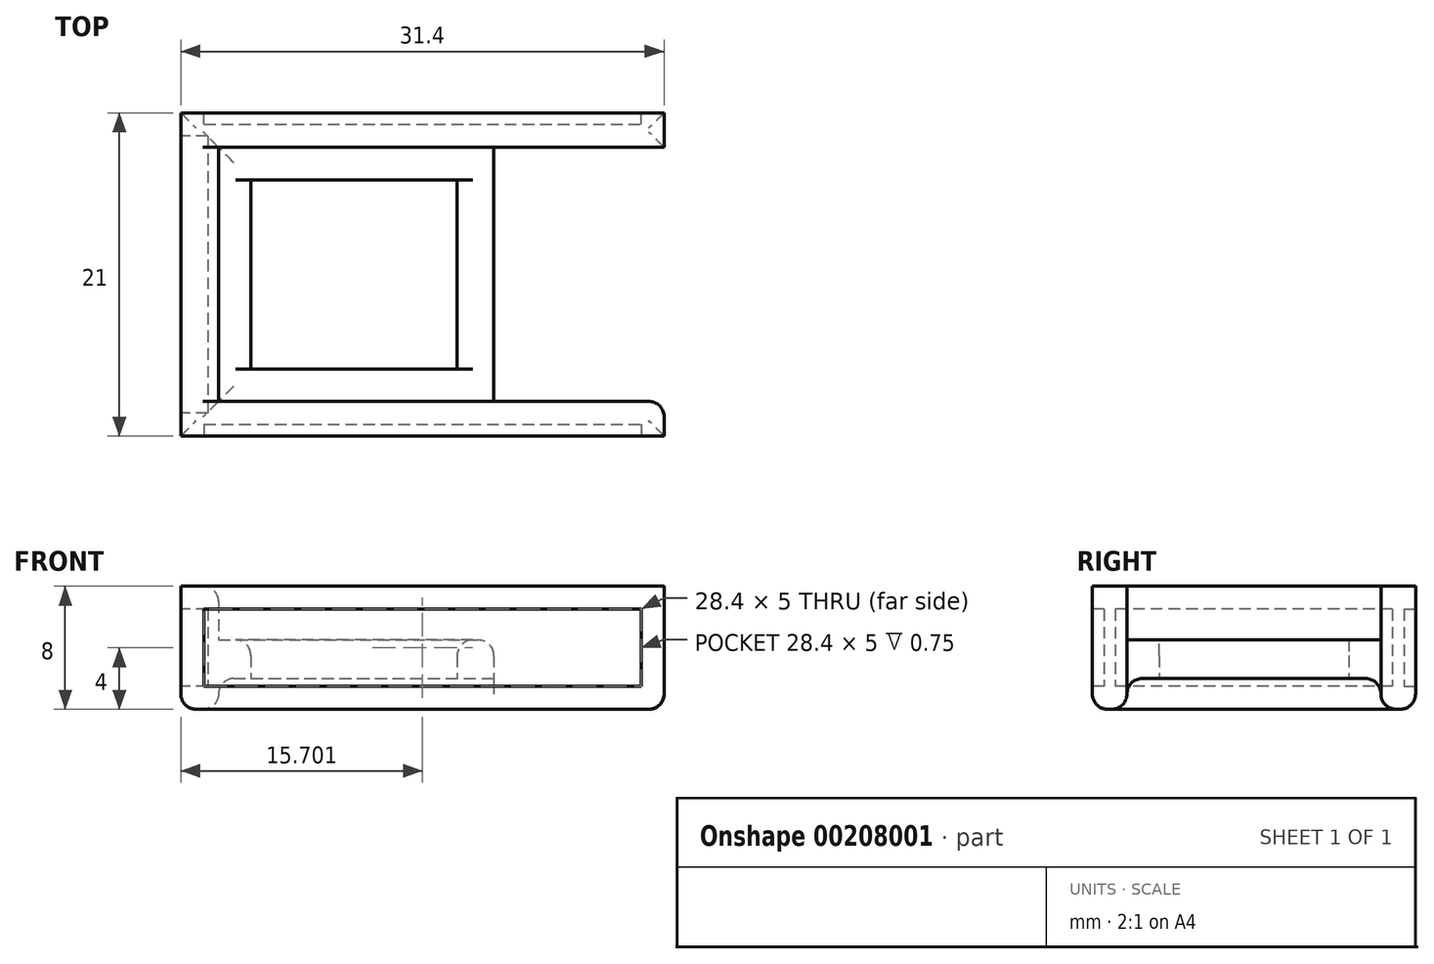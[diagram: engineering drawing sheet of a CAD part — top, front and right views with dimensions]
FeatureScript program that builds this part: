
annotation { "Feature Type Name" : "Feature", "Feature Type Description" : "" }
export const myFeature = defineFeature(function(context is Context, id is Id, definition is map)
    precondition{}
    {
        {
            var Q0;
            Q0=qCreatedBy(makeId("Top.planeOp"),FACE);
            var sketch = newSketch(context, id + "F0", { "sketchPlane" : qUnion([Q0])});
            skLineSegment(sketch, "E0.right", {"start": v(-20, 11.13) * mm, "end": v(-20, -11.87) * mm});
            skLineSegment(sketch, "E1", {"start": v(9.95, 7.88) * mm, "end": v(9.95, -8.62) * mm});
            skPoint(sketch, "E2.orphan", {"position": v(-20, -0.37) * mm});
            skPoint(sketch, "E3.end.orphan", {"position": v(-16.55, -1.12) * mm});
            skLineSegment(sketch, "E4", {"start": v(-16.55, 7.88) * mm, "end": v(-16.55, -8.62) * mm});
            skLineSegment(sketch, "E5", {"start": v(13.4, 11.13) * mm, "end": v(13.4, -11.87) * mm});
            skLineSegment(sketch, "E6", {"start": v(-20, 11.13) * mm, "end": v(13.4, 11.13) * mm});
            skLineSegment(sketch, "E7", {"start": v(-20, -11.87) * mm, "end": v(13.4, -11.87) * mm});
            skLineSegment(sketch, "E8", {"start": v(-16.55, 7.88) * mm, "end": v(9.95, 7.88) * mm});
            skLineSegment(sketch, "E9", {"start": v(-16.55, -8.62) * mm, "end": v(9.95, -8.62) * mm});
            skLineSegment(sketch, "E10", {"start": v(1.34, 7.88) * mm, "end": v(1.34, -8.62) * mm});
            skSolve(sketch);
        }
        {
            var Q0;
            Q0=makeQuery(id+"F0.imprint","IMPRINT",FACE,{"disambiguationData":[TD([[makeQuery(id+"F0.imprint","IMPRINT",EDGE,{"derivedFrom":sQuery(id+"F0.wireOp",EDGE,"E0.right")}),1.0]])]});
            extrude(context, id + "F1", {"entities" : qUnion([Q0]), "depth" : 8 * mm});
        }
        {
            var Q0;
            {var subQ0=sQuery(id+"F0.wireOp",EDGE,"E4");Q0=makeQuery(id+"F0.imprint","IMPRINT",FACE,{"disambiguationData":[TD([[makeQuery(id+"F0.imprint","IMPRINT",EDGE,{"derivedFrom":subQ0}),1.0]])]});}
            extrude(context, id + "F2", {"entities" : qUnion([Q0]), "operationType" : NewBodyOperationType.ADD, "depth" : 4.5 * mm});
        }
        {
            var Q0;
            Q0=makeQuery(id+"F1.opExtrude","SWEPT_FACE",FACE,{"disambiguationData":[OSD([sQuery(id+"F0.wireOp",EDGE,"E7")])]});
            extrude(context, id + "F3", {"entities" : qUnion([Q0]), "operationType" : NewBodyOperationType.REMOVE, "oppositeDirection" : true, "depth" : 1 * mm});
        }
        {
            var Q0;
            Q0=makeQuery(id+"F1.opExtrude","SWEPT_FACE",FACE,{"disambiguationData":[OSD([sQuery(id+"F0.wireOp",EDGE,"E5")])]});
            extrude(context, id + "F4", {"entities" : qUnion([Q0]), "operationType" : NewBodyOperationType.REMOVE, "oppositeDirection" : true, "depth" : 1 * mm});
        }
        {
            var Q0;
            Q0=makeQuery(id+"F1.opExtrude","SWEPT_FACE",FACE,{"disambiguationData":[OSD([sQuery(id+"F0.wireOp",EDGE,"E6")])]});
            extrude(context, id + "F5", {"entities" : qUnion([Q0]), "operationType" : NewBodyOperationType.REMOVE, "oppositeDirection" : true, "depth" : 1 * mm});
        }
        {
            var Q0;
            Q0=makeQuery(id+"F1.opExtrude","SWEPT_FACE",FACE,{"disambiguationData":[OSD([sQuery(id+"F0.wireOp",EDGE,"E0.right")])]});
            extrude(context, id + "F6", {"entities" : qUnion([Q0]), "operationType" : NewBodyOperationType.REMOVE, "oppositeDirection" : true, "depth" : 1 * mm});
        }
        {
            var Q0;
            {var subQ0=sQuery(id+"F0.wireOp",EDGE,"E4");Q0=makeQuery(id+"F0.imprint","IMPRINT",FACE,{"disambiguationData":[TD([[makeQuery(id+"F0.imprint","IMPRINT",EDGE,{"derivedFrom":subQ0}),1.0]])]});}
            extrude(context, id + "F7", {"entities" : qUnion([Q0]), "operationType" : NewBodyOperationType.REMOVE, "depth" : 2 * mm});
        }
        {
            var Q0;
            Q0=makeQuery(id+"F7.boolean.opBoolean","COPY",FACE,{"derivedFrom":makeQuery(id+"F7.opExtrude","CAP_FACE",FACE,{"disambiguationData":[OSD([sQuery(id+"F0.wireOp",EDGE,"E4"),sQuery(id+"F0.wireOp",EDGE,"E8"),sQuery(id+"F0.wireOp",EDGE,"E9"),sQuery(id+"F0.wireOp",EDGE,"sh9WD1Uu-prVP-sZlt-RPRa-mIaGXH6vvo3p")])],"isStart":false})});
            var sketch = newSketch(context, id + "F8", { "sketchPlane" : qUnion([Q0])});
            skPoint(sketch, "E11.centerSnap0", {"position": v(-7.6, 8.62) * mm});
            skLineSegment(sketch, "E12.1", {"start": v(-14.45, -5.77) * mm, "end": v(-14.45, 6.52) * mm});
            skLineSegment(sketch, "E12.3", {"start": v(-1.05, -5.77) * mm, "end": v(-1.05, 6.52) * mm});
            skLineSegment(sketch, "E13", {"start": v(-14.45, -5.77) * mm, "end": v(-1.05, -5.77) * mm});
            skLineSegment(sketch, "E14", {"start": v(-14.45, 6.52) * mm, "end": v(-1.05, 6.52) * mm});
            skPoint(sketch, "E11.center.orphan", {"position": v(-7.6, 0) * mm});
            skSolve(sketch);
        }
        {
            var Q0;
            Q0=makeQuery(id+"F8.imprint","IMPRINT",FACE,{"disambiguationData":[TD([[makeQuery(id+"F8.imprint","IMPRINT",EDGE,{"derivedFrom":sQuery(id+"F8.wireOp",EDGE,"E12.1")}),-1.0]])]});
            extrude(context, id + "F9", {"entities" : qUnion([Q0]), "operationType" : NewBodyOperationType.REMOVE, "oppositeDirection" : true, "depth" : 3.4 * mm});
        }
        {
            var Q0;
            Q0=makeQuery(id+"F4.boolean.opBoolean","COPY",FACE,{"derivedFrom":makeQuery(id+"F4.opExtrude","CAP_FACE",FACE,{"disambiguationData":[OSD([sQuery(id+"F0.wireOp",EDGE,"E5")])],"isStart":false})});
            var sketch = newSketch(context, id + "F10", { "sketchPlane" : qUnion([Q0])});
            skLineSegment(sketch, "E15.0", {"start": v(10.13, 8) * mm, "end": v(-10.87, 8) * mm});
            skLineSegment(sketch, "E15.1", {"start": v(-10.87, 8) * mm, "end": v(-10.87, 0) * mm});
            skLineSegment(sketch, "E15.2", {"start": v(10.13, 0) * mm, "end": v(7.88, 0) * mm});
            skLineSegment(sketch, "E15.3", {"start": v(10.13, 8) * mm, "end": v(10.13, 0) * mm});
            skPoint(sketch, "E16.end.orphan", {"position": v(-9.38, 8) * mm});
            skPoint(sketch, "E17.end.orphan", {"position": v(8.63, 8) * mm});
            skPoint(sketch, "E18.end.orphan", {"position": v(-8.62, 8) * mm});
            skPoint(sketch, "E19.start.orphan", {"position": v(-8.62, 1) * mm});
            skLineSegment(sketch, "E20", {"start": v(-8.62, 8) * mm, "end": v(-8.62, 0) * mm});
            skLineSegment(sketch, "E21.trimOffspring", {"start": v(-8.62, 0) * mm, "end": v(-10.87, 0) * mm});
            skPoint(sketch, "E22.start.orphan", {"position": v(7.88, 1) * mm});
            skLineSegment(sketch, "E23", {"start": v(7.88, 0) * mm, "end": v(7.88, 8) * mm});
            skLineSegment(sketch, "E24", {"start": v(-8.62, 0) * mm, "end": v(7.88, 0) * mm});
            skLineSegment(sketch, "E25", {"start": v(-8.62, 8) * mm, "end": v(7.88, 8) * mm});
            skSolve(sketch);
        }
        {
            var Q0;
            Q0=makeQuery(id+"F3.boolean.opBoolean","COPY",FACE,{"derivedFrom":makeQuery(id+"F3.opExtrude","CAP_FACE",FACE,{"disambiguationData":[OSD([sQuery(id+"F0.wireOp",EDGE,"E7")])],"isStart":false})});
            var sketch = newSketch(context, id + "F11", { "sketchPlane" : qUnion([Q0])});
            skLineSegment(sketch, "E26.0", {"start": v(-19, 8) * mm, "end": v(12.4, 8) * mm});
            skLineSegment(sketch, "E26.1", {"start": v(-19, 8) * mm, "end": v(-19, 0) * mm});
            skLineSegment(sketch, "E26.2", {"start": v(-19, 0) * mm, "end": v(12.4, 0) * mm});
            skLineSegment(sketch, "E26.3", {"start": v(12.4, 8) * mm, "end": v(12.4, 0) * mm});
            skLineSegment(sketch, "E27.0", {"start": v(-17.5, 6.5) * mm, "end": v(10.9, 6.5) * mm});
            skLineSegment(sketch, "E27.1", {"start": v(-17.5, 6.5) * mm, "end": v(-17.5, 1.5) * mm});
            skLineSegment(sketch, "E27.2", {"start": v(-17.5, 1.5) * mm, "end": v(10.9, 1.5) * mm});
            skLineSegment(sketch, "E27.3", {"start": v(10.9, 6.5) * mm, "end": v(10.9, 1.5) * mm});
            skSolve(sketch);
        }
        {
            var Q0;
            Q0=makeQuery(id+"F11.imprint","IMPRINT",FACE,{"disambiguationData":[TD([[makeQuery(id+"F11.imprint","IMPRINT",EDGE,{"derivedFrom":sQuery(id+"F11.wireOp",EDGE,"E27.0")}),-1.0]])]});
            extrude(context, id + "F12", {"entities" : qUnion([Q0]), "operationType" : NewBodyOperationType.REMOVE, "oppositeDirection" : true, "depth" : .75 * mm});
        }
        {
            var Q0;
            Q0=makeQuery(id+"F5.boolean.opBoolean","COPY",FACE,{"derivedFrom":makeQuery(id+"F5.opExtrude","CAP_FACE",FACE,{"disambiguationData":[OSD([sQuery(id+"F0.wireOp",EDGE,"E6")])],"isStart":false})});
            var sketch = newSketch(context, id + "F13", { "sketchPlane" : qUnion([Q0])});
            skLineSegment(sketch, "E28.0", {"start": v(19, 8) * mm, "end": v(-12.4, 8) * mm});
            skLineSegment(sketch, "E28.1", {"start": v(-12.4, 8) * mm, "end": v(-12.4, 0) * mm});
            skLineSegment(sketch, "E28.2", {"start": v(19, 0) * mm, "end": v(-12.4, 0) * mm});
            skLineSegment(sketch, "E28.3", {"start": v(19, 8) * mm, "end": v(19, 0) * mm});
            skLineSegment(sketch, "E29.0", {"start": v(17.5, 6.5) * mm, "end": v(-10.9, 6.5) * mm});
            skLineSegment(sketch, "E29.1", {"start": v(17.5, 6.5) * mm, "end": v(17.5, 1.5) * mm});
            skLineSegment(sketch, "E29.2", {"start": v(17.5, 1.5) * mm, "end": v(-10.9, 1.5) * mm});
            skLineSegment(sketch, "E29.3", {"start": v(-10.9, 6.5) * mm, "end": v(-10.9, 1.5) * mm});
            skSolve(sketch);
        }
        {
            var Q0;
            Q0=makeQuery(id+"F13.imprint","IMPRINT",FACE,{"disambiguationData":[TD([[makeQuery(id+"F13.imprint","IMPRINT",EDGE,{"derivedFrom":sQuery(id+"F13.wireOp",EDGE,"E29.0")}),1.0]])]});
            extrude(context, id + "F14", {"entities" : qUnion([Q0]), "operationType" : NewBodyOperationType.REMOVE, "oppositeDirection" : true, "depth" : .75 * mm});
        }
        {
            var Q0;
            Q0=makeQuery(id+"F6.boolean.opBoolean","COPY",FACE,{"derivedFrom":makeQuery(id+"F6.opExtrude","CAP_FACE",FACE,{"disambiguationData":[OSD([sQuery(id+"F0.wireOp",EDGE,"E0.right")])],"isStart":false})});
            var sketch = newSketch(context, id + "F15", { "sketchPlane" : qUnion([Q0])});
            skLineSegment(sketch, "E30.0", {"start": v(-10.13, 8) * mm, "end": v(10.87, 8) * mm});
            skLineSegment(sketch, "E30.1", {"start": v(-10.13, 8) * mm, "end": v(-10.13, 0) * mm});
            skLineSegment(sketch, "E30.2", {"start": v(-10.13, 0) * mm, "end": v(10.87, 0) * mm});
            skLineSegment(sketch, "E30.3", {"start": v(10.87, 8) * mm, "end": v(10.87, 0) * mm});
            skLineSegment(sketch, "E31.0", {"start": v(-8.63, 6.5) * mm, "end": v(9.37, 6.5) * mm});
            skLineSegment(sketch, "E31.1", {"start": v(-8.63, 6.5) * mm, "end": v(-8.63, 1.5) * mm});
            skLineSegment(sketch, "E31.2", {"start": v(-8.63, 1.5) * mm, "end": v(9.37, 1.5) * mm});
            skLineSegment(sketch, "E31.3", {"start": v(9.37, 6.5) * mm, "end": v(9.37, 1.5) * mm});
            skSolve(sketch);
        }
        {
            var Q0;
            Q0=makeQuery(id+"F15.imprint","IMPRINT",FACE,{"disambiguationData":[TD([[makeQuery(id+"F15.imprint","IMPRINT",EDGE,{"derivedFrom":sQuery(id+"F15.wireOp",EDGE,"E31.0")}),-1.0]])]});
            extrude(context, id + "F16", {"entities" : qUnion([Q0]), "operationType" : NewBodyOperationType.REMOVE, "oppositeDirection" : true, "depth" : 1.75 * mm});
        }
        {
            var Q0;
            Q0=makeQuery(id+"F10.imprint","IMPRINT",FACE,{"disambiguationData":[TD([[makeQuery(id+"F10.imprint","IMPRINT",EDGE,{"derivedFrom":sQuery(id+"F10.wireOp",EDGE,"b7a4e5c1-38a7-4f7a-ade6-748fce616738.0")}),1.0]])]});
            var Q1;
            Q1=makeQuery(id+"F10.imprint","IMPRINT",FACE,{"disambiguationData":[TD([[makeQuery(id+"F10.imprint","IMPRINT",EDGE,{"derivedFrom":sQuery(id+"F10.wireOp",EDGE,"zXJZTFNW-ofoD-sTrx-fMxL-tEjjA4OFiIrL")}),1.0]])]});
            var Q2;
            {var subQ1=sQuery(id+"F10.wireOp",EDGE,"MFRXstpn-q3tD-Dd6x-ulRt-eHmqPIAjv6JT");Q2=makeQuery(id+"F10.imprint","IMPRINT",FACE,{"disambiguationData":[TD([[makeQuery(id+"F10.imprint","IMPRINT",EDGE,{"derivedFrom":subQ1}),1.0]])]});}
            var Q3;
            Q3=makeQuery(id+"F10.imprint","IMPRINT",FACE,{"disambiguationData":[TD([[makeQuery(id+"F10.imprint","IMPRINT",EDGE,{"derivedFrom":sQuery(id+"F10.wireOp",EDGE,"E20")}),1.0]])]});
            extrude(context, id + "F17", {"entities" : qUnion([Q0, Q1, Q2, Q3]), "operationType" : NewBodyOperationType.REMOVE, "oppositeDirection" : true, "depth" : 2.5 * mm});
        }
        {
            var Q0;
            {var subQ0=sQuery(id+"F0.wireOp",EDGE,"E6");Q0=makeQuery(id+"F5.boolean.opBoolean","COPY",EDGE,{"derivedFrom":makeQuery(id+"F5.opExtrude","CAP_EDGE",EDGE,{"disambiguationData":[OSD([subQ0]),TDD([makeQuery(id+"F1.opExtrude","CAP_EDGE",EDGE,{"disambiguationData":[OSD([subQ0])],"isStart":false})])],"isStart":false})});}
            var Q1;
            Q1=makeQuery(id+"F17.boolean.opBoolean","MERGE",EDGE,{"derivedFrom":[makeQuery(id+"F1.opExtrude","CAP_EDGE",EDGE,{"disambiguationData":[OSD([sQuery(id+"F0.wireOp",EDGE,"E8")])],"isStart":false}),makeQuery(id+"F17.opExtrude","SWEPT_EDGE",EDGE,{"disambiguationData":[OSD([sQuery(id+"F10.wireOp",EDGE,"E15.0"),sQuery(id+"F10.wireOp",EDGE,"E23"),sQuery(id+"F10.wireOp",EDGE,"E25")])]})]});
            var Q2;
            {var subQ0=sQuery(id+"F0.wireOp",EDGE,"E0.right");Q2=makeQuery(id+"F6.boolean.opBoolean","COPY",EDGE,{"derivedFrom":makeQuery(id+"F6.opExtrude","CAP_EDGE",EDGE,{"disambiguationData":[OSD([subQ0]),TDD([makeQuery(id+"F1.opExtrude","CAP_EDGE",EDGE,{"disambiguationData":[OSD([subQ0])],"isStart":false})])],"isStart":false})});}
            var Q3;
            Q3=makeQuery(id+"F1.opExtrude","CAP_EDGE",EDGE,{"disambiguationData":[OSD([sQuery(id+"F0.wireOp",EDGE,"E4")])],"isStart":false});
            var Q4;
            Q4=makeQuery(id+"F17.boolean.opBoolean","MERGE",EDGE,{"derivedFrom":[makeQuery(id+"F1.opExtrude","CAP_EDGE",EDGE,{"disambiguationData":[OSD([sQuery(id+"F0.wireOp",EDGE,"E9")])],"isStart":false}),makeQuery(id+"F17.opExtrude","SWEPT_EDGE",EDGE,{"disambiguationData":[OSD([sQuery(id+"F10.wireOp",EDGE,"E15.0"),sQuery(id+"F10.wireOp",EDGE,"E20"),sQuery(id+"F10.wireOp",EDGE,"E25")])]})]});
            var Q5;
            {var subQ0=sQuery(id+"F0.wireOp",EDGE,"E7");Q5=makeQuery(id+"F3.boolean.opBoolean","COPY",EDGE,{"derivedFrom":makeQuery(id+"F3.opExtrude","CAP_EDGE",EDGE,{"disambiguationData":[OSD([subQ0]),TDD([makeQuery(id+"F1.opExtrude","CAP_EDGE",EDGE,{"disambiguationData":[OSD([subQ0])],"isStart":false})])],"isStart":false})});}
            var Q6;
            {var subQ0=sQuery(id+"F0.wireOp",EDGE,"E5");var subQ2=sQuery(id+"F0.wireOp",EDGE,"E9");Q6=makeQuery(id+"F17.boolean.opBoolean","SPLIT",EDGE,{"disambiguationData":[TD([makeQuery(id+"F1.opExtrude","SWEPT_FACE",FACE,{"disambiguationData":[OSD([subQ2])]})])],"derivedFrom":makeQuery(id+"F4.boolean.opBoolean","COPY",EDGE,{"derivedFrom":makeQuery(id+"F4.opExtrude","CAP_EDGE",EDGE,{"disambiguationData":[OSD([subQ0]),TDD([makeQuery(id+"F1.opExtrude","CAP_EDGE",EDGE,{"disambiguationData":[OSD([subQ0])],"isStart":false})])],"isStart":false})})});}
            var Q7;
            {var subQ1=sQuery(id+"F0.wireOp",EDGE,"E5");var subQ2=sQuery(id+"F0.wireOp",EDGE,"E8");Q7=makeQuery(id+"F17.boolean.opBoolean","SPLIT",EDGE,{"disambiguationData":[TD([makeQuery(id+"F1.opExtrude","SWEPT_FACE",FACE,{"disambiguationData":[OSD([subQ2])]})])],"derivedFrom":makeQuery(id+"F4.boolean.opBoolean","COPY",EDGE,{"derivedFrom":makeQuery(id+"F4.opExtrude","CAP_EDGE",EDGE,{"disambiguationData":[OSD([subQ1]),TDD([makeQuery(id+"F1.opExtrude","CAP_EDGE",EDGE,{"disambiguationData":[OSD([subQ1])],"isStart":false})])],"isStart":false})})});}
            var Q8;
            {var subQ0=sQuery(id+"F0.wireOp",EDGE,"E5");var subQ2=sQuery(id+"F0.wireOp",EDGE,"E8");Q8=makeQuery(id+"F17.boolean.opBoolean","SPLIT",EDGE,{"disambiguationData":[TD([makeQuery(id+"F1.opExtrude","SWEPT_FACE",FACE,{"disambiguationData":[OSD([subQ2])]})])],"derivedFrom":makeQuery(id+"F4.boolean.opBoolean","COPY",EDGE,{"derivedFrom":makeQuery(id+"F4.opExtrude","CAP_EDGE",EDGE,{"disambiguationData":[OSD([subQ0]),TDD([makeQuery(id+"F1.opExtrude","CAP_EDGE",EDGE,{"disambiguationData":[OSD([subQ0])],"isStart":true})])],"isStart":false})})});}
            var Q9;
            {var subQ1=sQuery(id+"F0.wireOp",EDGE,"E9");var subQ4=sQuery(id+"F0.wireOp",EDGE,"E5");Q9=makeQuery(id+"F17.boolean.opBoolean","SPLIT",EDGE,{"disambiguationData":[TD([makeQuery(id+"F1.opExtrude","SWEPT_FACE",FACE,{"disambiguationData":[OSD([subQ1])]})])],"derivedFrom":makeQuery(id+"F4.boolean.opBoolean","COPY",EDGE,{"derivedFrom":makeQuery(id+"F4.opExtrude","CAP_EDGE",EDGE,{"disambiguationData":[OSD([subQ4]),TDD([makeQuery(id+"F1.opExtrude","CAP_EDGE",EDGE,{"disambiguationData":[OSD([subQ4])],"isStart":true})])],"isStart":false})})});}
            var Q10;
            {var subQ0=sQuery(id+"F0.wireOp",EDGE,"E6");Q10=makeQuery(id+"F5.boolean.opBoolean","COPY",EDGE,{"derivedFrom":makeQuery(id+"F5.opExtrude","CAP_EDGE",EDGE,{"disambiguationData":[OSD([subQ0]),TDD([makeQuery(id+"F1.opExtrude","CAP_EDGE",EDGE,{"disambiguationData":[OSD([subQ0])],"isStart":true})])],"isStart":false})});}
            var Q11;
            {var subQ0=sQuery(id+"F0.wireOp",EDGE,"E7");Q11=makeQuery(id+"F3.boolean.opBoolean","COPY",EDGE,{"derivedFrom":makeQuery(id+"F3.opExtrude","CAP_EDGE",EDGE,{"disambiguationData":[OSD([subQ0]),TDD([makeQuery(id+"F1.opExtrude","CAP_EDGE",EDGE,{"disambiguationData":[OSD([subQ0])],"isStart":true})])],"isStart":false})});}
            var Q12;
            {var subQ0=sQuery(id+"F0.wireOp",EDGE,"E9");var subQ1=sQuery(id+"F0.wireOp",EDGE,"E8");var subQ2=sQuery(id+"F0.wireOp",EDGE,"E4");Q12=makeQuery(id+"F2.boolean.opBoolean","MERGE",FACE,{"derivedFrom":[makeQuery(id+"F1.opExtrude","CAP_FACE",FACE,{"disambiguationData":[OSD([sQuery(id+"F0.wireOp",EDGE,"E0.right"),sQuery(id+"F0.wireOp",EDGE,"E1"),subQ2,sQuery(id+"F0.wireOp",EDGE,"E5"),sQuery(id+"F0.wireOp",EDGE,"E6"),sQuery(id+"F0.wireOp",EDGE,"E7"),subQ1,subQ0])],"isStart":true}),makeQuery(id+"F2.opExtrude","CAP_FACE",FACE,{"disambiguationData":[OSD([subQ2,subQ1,subQ0,sQuery(id+"F0.wireOp",EDGE,"sh9WD1Uu-prVP-sZlt-RPRa-mIaGXH6vvo3p")])],"isStart":true})]});}
            var Q13;
            {var subQ0=sQuery(id+"F0.wireOp",EDGE,"E8");Q13=makeQuery(id+"F17.boolean.opBoolean","MERGE",EDGE,{"derivedFrom":[makeQuery(id+"F7.boolean.opBoolean","MERGE",EDGE,{"derivedFrom":[makeQuery(id+"F1.opExtrude","CAP_EDGE",EDGE,{"disambiguationData":[OSD([subQ0])],"isStart":true}),makeQuery(id+"F7.opExtrude","CAP_EDGE",EDGE,{"disambiguationData":[OSD([subQ0])],"isStart":true})]}),makeQuery(id+"F17.opExtrude","SWEPT_EDGE",EDGE,{"disambiguationData":[OSD([sQuery(id+"F10.wireOp",EDGE,"E15.2"),sQuery(id+"F10.wireOp",EDGE,"E23"),sQuery(id+"F10.wireOp",EDGE,"E24")])]})]});}
            var Q14;
            Q14=makeQuery(id+"F4.boolean.opBoolean","COPY",EDGE,{"derivedFrom":makeQuery(id+"F4.opExtrude","CAP_EDGE",EDGE,{"disambiguationData":[OSD([sQuery(id+"F0.wireOp",EDGE,"E5"),sQuery(id+"F0.wireOp",EDGE,"E7")])],"isStart":false})});
            var Q15;
            Q15=makeQuery(id+"F17.boolean.opBoolean","COPY",EDGE,{"derivedFrom":makeQuery(id+"F17.opExtrude","CAP_EDGE",EDGE,{"disambiguationData":[OSD([sQuery(id+"F10.wireOp",EDGE,"E20")])],"isStart":true})});
            var Q16;
            Q16=makeQuery(id+"F17.boolean.opBoolean","COPY",EDGE,{"derivedFrom":makeQuery(id+"F17.opExtrude","CAP_EDGE",EDGE,{"disambiguationData":[OSD([sQuery(id+"F10.wireOp",EDGE,"E23")])],"isStart":true})});
            var Q17;
            Q17=makeQuery(id+"F5.boolean.opBoolean","COPY",EDGE,{"derivedFrom":makeQuery(id+"F5.opExtrude","CAP_EDGE",EDGE,{"disambiguationData":[OSD([sQuery(id+"F0.wireOp",EDGE,"E5"),sQuery(id+"F0.wireOp",EDGE,"E6")])],"isStart":false})});
            var Q18;
            Q18=makeQuery(id+"F6.boolean.opBoolean","COPY",EDGE,{"derivedFrom":makeQuery(id+"F6.opExtrude","CAP_EDGE",EDGE,{"disambiguationData":[OSD([sQuery(id+"F0.wireOp",EDGE,"E0.right"),sQuery(id+"F0.wireOp",EDGE,"E7")])],"isStart":false})});
            var Q19;
            Q19=makeQuery(id+"F6.boolean.opBoolean","COPY",EDGE,{"derivedFrom":makeQuery(id+"F6.opExtrude","CAP_EDGE",EDGE,{"disambiguationData":[OSD([sQuery(id+"F0.wireOp",EDGE,"E0.right"),sQuery(id+"F0.wireOp",EDGE,"E6")])],"isStart":false})});
            var Q20;
            Q20=makeQuery(id+"F9.boolean.opBoolean","INTERSECT",EDGE,{"derivedFrom":[makeQuery(id+"F2.opExtrude","CAP_FACE",FACE,{"disambiguationData":[OSD([sQuery(id+"F0.wireOp",EDGE,"E4"),sQuery(id+"F0.wireOp",EDGE,"E8"),sQuery(id+"F0.wireOp",EDGE,"E9"),sQuery(id+"F0.wireOp",EDGE,"sh9WD1Uu-prVP-sZlt-RPRa-mIaGXH6vvo3p")])],"isStart":false}),makeQuery(id+"F9.opExtrude","SWEPT_FACE",FACE,{"disambiguationData":[OSD([sQuery(id+"F8.wireOp",EDGE,"E12.2")])]})]});
            var Q21;
            Q21=makeQuery(id+"F9.boolean.opBoolean","INTERSECT",EDGE,{"derivedFrom":[makeQuery(id+"F2.opExtrude","CAP_FACE",FACE,{"disambiguationData":[OSD([sQuery(id+"F0.wireOp",EDGE,"E4"),sQuery(id+"F0.wireOp",EDGE,"E8"),sQuery(id+"F0.wireOp",EDGE,"E9"),sQuery(id+"F0.wireOp",EDGE,"sh9WD1Uu-prVP-sZlt-RPRa-mIaGXH6vvo3p")])],"isStart":false}),makeQuery(id+"F9.opExtrude","SWEPT_FACE",FACE,{"disambiguationData":[OSD([sQuery(id+"F8.wireOp",EDGE,"E12.1")])]})]});
            var Q22;
            Q22=makeQuery(id+"F9.boolean.opBoolean","INTERSECT",EDGE,{"derivedFrom":[makeQuery(id+"F2.opExtrude","CAP_FACE",FACE,{"disambiguationData":[OSD([sQuery(id+"F0.wireOp",EDGE,"E4"),sQuery(id+"F0.wireOp",EDGE,"E8"),sQuery(id+"F0.wireOp",EDGE,"E9"),sQuery(id+"F0.wireOp",EDGE,"sh9WD1Uu-prVP-sZlt-RPRa-mIaGXH6vvo3p")])],"isStart":false}),makeQuery(id+"F9.opExtrude","SWEPT_FACE",FACE,{"disambiguationData":[OSD([sQuery(id+"F8.wireOp",EDGE,"E12.3")])]})]});
            var Q23;
            Q23=makeQuery(id+"F2.opExtrude","CAP_EDGE",EDGE,{"disambiguationData":[OSD([sQuery(id+"F0.wireOp",EDGE,"sh9WD1Uu-prVP-sZlt-RPRa-mIaGXH6vvo3p")])],"isStart":false});
            var Q24;
            Q24=makeQuery(id+"F9.boolean.opBoolean","INTERSECT",EDGE,{"derivedFrom":[makeQuery(id+"F2.opExtrude","CAP_FACE",FACE,{"disambiguationData":[OSD([sQuery(id+"F0.wireOp",EDGE,"E4"),sQuery(id+"F0.wireOp",EDGE,"E8"),sQuery(id+"F0.wireOp",EDGE,"E9"),sQuery(id+"F0.wireOp",EDGE,"sh9WD1Uu-prVP-sZlt-RPRa-mIaGXH6vvo3p")])],"isStart":false}),makeQuery(id+"F9.opExtrude","SWEPT_FACE",FACE,{"disambiguationData":[OSD([sQuery(id+"F8.wireOp",EDGE,"E12.0")])]})]});
            var Q25;
            Q25=makeQuery(id+"F7.boolean.opBoolean","COPY",EDGE,{"derivedFrom":makeQuery(id+"F7.opExtrude","CAP_EDGE",EDGE,{"disambiguationData":[OSD([sQuery(id+"F0.wireOp",EDGE,"sh9WD1Uu-prVP-sZlt-RPRa-mIaGXH6vvo3p")])],"isStart":false})});
            var Q26;
            Q26=makeQuery(id+"F7.boolean.opBoolean","COPY",EDGE,{"derivedFrom":makeQuery(id+"F7.opExtrude","CAP_EDGE",EDGE,{"disambiguationData":[OSD([sQuery(id+"F0.wireOp",EDGE,"E8")])],"isStart":false})});
            var Q27;
            Q27=makeQuery(id+"F7.boolean.opBoolean","COPY",EDGE,{"derivedFrom":makeQuery(id+"F7.opExtrude","CAP_EDGE",EDGE,{"disambiguationData":[OSD([sQuery(id+"F0.wireOp",EDGE,"E4")])],"isStart":false})});
            var Q28;
            Q28=makeQuery(id+"F7.boolean.opBoolean","COPY",EDGE,{"derivedFrom":makeQuery(id+"F7.opExtrude","CAP_EDGE",EDGE,{"disambiguationData":[OSD([sQuery(id+"F0.wireOp",EDGE,"E9")])],"isStart":false})});
            var Q29;
            Q29=makeQuery(id+"F9.boolean.opBoolean","COPY",EDGE,{"derivedFrom":makeQuery(id+"F9.opExtrude","CAP_EDGE",EDGE,{"disambiguationData":[OSD([sQuery(id+"F8.wireOp",EDGE,"E12.3")])],"isStart":true})});
            var Q30;
            Q30=makeQuery(id+"F9.boolean.opBoolean","COPY",EDGE,{"derivedFrom":makeQuery(id+"F9.opExtrude","CAP_EDGE",EDGE,{"disambiguationData":[OSD([sQuery(id+"F8.wireOp",EDGE,"E12.0")])],"isStart":true})});
            var Q31;
            Q31=makeQuery(id+"F9.boolean.opBoolean","COPY",EDGE,{"derivedFrom":makeQuery(id+"F9.opExtrude","CAP_EDGE",EDGE,{"disambiguationData":[OSD([sQuery(id+"F8.wireOp",EDGE,"E12.1")])],"isStart":true})});
            var Q32;
            Q32=makeQuery(id+"F9.boolean.opBoolean","COPY",EDGE,{"derivedFrom":makeQuery(id+"F9.opExtrude","CAP_EDGE",EDGE,{"disambiguationData":[OSD([sQuery(id+"F8.wireOp",EDGE,"E12.2")])],"isStart":true})});
            var Q33;
            Q33=makeQuery(id+"F2.opExtrude","CAP_EDGE",EDGE,{"disambiguationData":[OSD([sQuery(id+"F0.wireOp",EDGE,"E4")])],"isStart":false});
            var Q34;
            Q34=makeQuery(id+"F2.opExtrude","CAP_EDGE",EDGE,{"disambiguationData":[OSD([sQuery(id+"F0.wireOp",EDGE,"E10")])],"isStart":false});
            var Q35;
            Q35=makeQuery(id+"F7.boolean.opBoolean","COPY",EDGE,{"derivedFrom":makeQuery(id+"F7.opExtrude","CAP_EDGE",EDGE,{"disambiguationData":[OSD([sQuery(id+"F0.wireOp",EDGE,"E10")])],"isStart":false})});
            fillet(context, id + "F18", {"entities" : qUnion([Q0, Q1, Q2, Q3, Q4, Q5, Q6, Q7, Q8, Q9, Q10, Q11, Q12, Q13, Q14, Q15, Q16, Q17, Q18, Q19, Q20, Q21, Q22, Q23, Q24, Q25, Q26, Q27, Q28, Q29, Q30, Q31, Q32, Q33, Q34, Q35]), "radius" : 1 * mm, "tangentPropagation" : true, "allowEdgeOverflow" : false});
        }
    });
